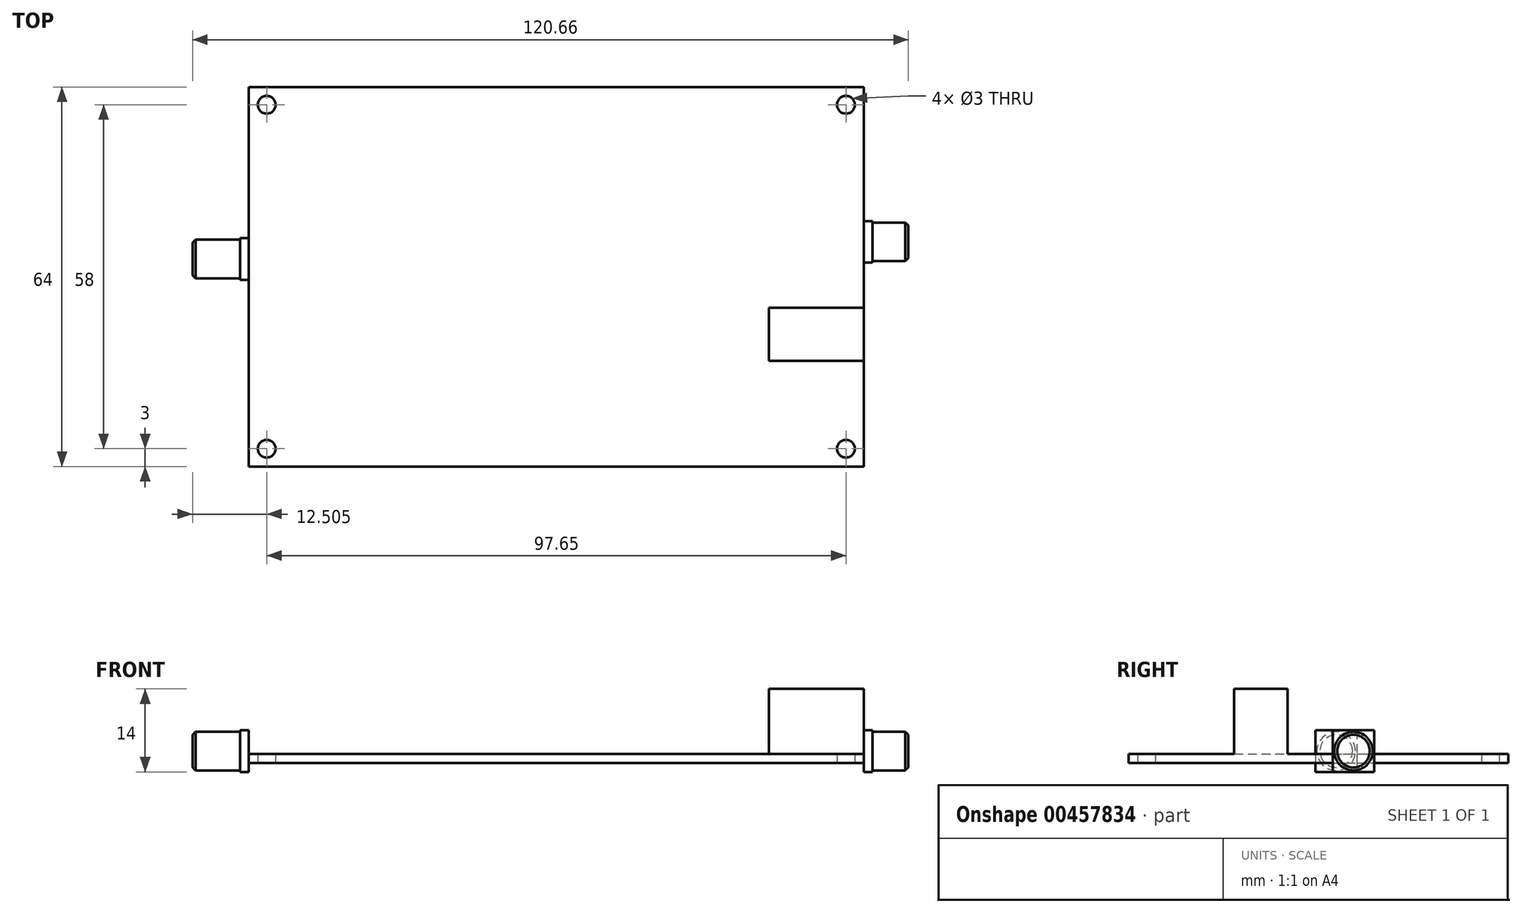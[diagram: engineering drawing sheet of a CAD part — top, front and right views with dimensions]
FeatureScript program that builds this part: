
annotation { "Feature Type Name" : "Feature", "Feature Type Description" : "" }
export const myFeature = defineFeature(function(context is Context, id is Id, definition is map)
    precondition{}
    {
        {
            var Q0;
            Q0=qCreatedBy(makeId("Top.planeOp"),FACE);
            var sketch = newSketch(context, id + "F0", { "sketchPlane" : qUnion([Q0])});
            skLineSegment(sketch, "E0.bottom", {"start": v(51.83, -32) * mm, "end": v(-51.82, -32) * mm});
            skLineSegment(sketch, "E0.top", {"start": v(51.83, 32) * mm, "end": v(-51.82, 32) * mm});
            skLineSegment(sketch, "E0.left", {"start": v(51.83, -32) * mm, "end": v(51.83, 32) * mm});
            skLineSegment(sketch, "E0.right", {"start": v(-51.83, -32) * mm, "end": v(-51.83, 32) * mm});
            skPoint(sketch, "E0.middle", {"position": v(0, 0) * mm});
            skCircle(sketch, "E1", {"center": v(-48.83, -29) * mm, "radius": 1.5 * mm});
            skCircle(sketch, "E2", {"center": v(-48.83, 29) * mm, "radius": 1.5 * mm});
            skCircle(sketch, "E3", {"center": v(48.82, 29) * mm, "radius": 1.5 * mm});
            skCircle(sketch, "E4", {"center": v(48.82, -29) * mm, "radius": 1.5 * mm});
            skSolve(sketch);
        }
        {
            var Q0;
            Q0=makeQuery(id+"F0.imprint","IMPRINT",FACE,{"disambiguationData":[TD([[makeQuery(id+"F0.imprint","IMPRINT",EDGE,{"derivedFrom":sQuery(id+"F0.wireOp",EDGE,"E0.bottom")}),-1.0]])]});
            extrude(context, id + "F1", {"entities" : qUnion([Q0]), "depth" : 1.5 * mm});
        }
        {
            var Q0;
            Q0=makeQuery(id+"F1.opExtrude","SWEPT_FACE",FACE,{"disambiguationData":[OSD([sQuery(id+"F0.wireOp",EDGE,"E0.left")])]});
            var sketch = newSketch(context, id + "F2", { "sketchPlane" : qUnion([Q0])});
            skLineSegment(sketch, "E5.bottom", {"start": v(-14.2, 1.5) * mm, "end": v(-5.2, 1.5) * mm});
            skLineSegment(sketch, "E5.top", {"start": v(-14.2, 12.5) * mm, "end": v(-5.2, 12.5) * mm});
            skLineSegment(sketch, "E5.left", {"start": v(-14.2, 1.5) * mm, "end": v(-14.2, 12.5) * mm});
            skLineSegment(sketch, "E5.right", {"start": v(-5.2, 1.5) * mm, "end": v(-5.2, 12.5) * mm});
            skSolve(sketch);
        }
        {
            var Q0;
            Q0=makeQuery(id+"F2.imprint","IMPRINT",FACE,{"disambiguationData":[TD([[makeQuery(id+"F2.imprint","IMPRINT",EDGE,{"derivedFrom":sQuery(id+"F2.wireOp",EDGE,"E5.bottom")}),1.0]])]});
            extrude(context, id + "F3", {"entities" : qUnion([Q0]), "operationType" : NewBodyOperationType.ADD, "oppositeDirection" : true, "depth" : 16 * mm});
        }
        {
            var Q0;
            {var subQ3=sQuery(id+"F2.wireOp",EDGE,"E5.bottom");Q0=makeQuery(id+"F2.imprint","IMPRINT",FACE,{"disambiguationData":[TD([[makeQuery(id+"F2.imprint","IMPRINT",EDGE,{"derivedFrom":subQ3}),-1.0]])]});}
            var sketch = newSketch(context, id + "F4", { "sketchPlane" : qUnion([Q0])});
            skLineSegment(sketch, "E6.bottom", {"start": v(2.4, 5.5) * mm, "end": v(9.4, 5.5) * mm});
            skLineSegment(sketch, "E6.top", {"start": v(2.4, -1.5) * mm, "end": v(9.4, -1.5) * mm});
            skLineSegment(sketch, "E6.left", {"start": v(2.4, 5.5) * mm, "end": v(2.4, -1.5) * mm});
            skLineSegment(sketch, "E6.right", {"start": v(9.4, 5.5) * mm, "end": v(9.4, -1.5) * mm});
            skSolve(sketch);
        }
        {
            var Q0;
            Q0 = qSketchRegion(id + "F4", true);
            var Q1;
            {var subQ0=sQuery(id+"F4.wireOp",EDGE,"E6.bottom");Q1=makeQuery(id+"F4.imprint","IMPRINT",FACE,{"disambiguationData":[TD([[makeQuery(id+"F4.imprint","IMPRINT",EDGE,{"derivedFrom":subQ0}),-1.0]])]});}
            extrude(context, id + "F5", {"entities" : qUnion([Q0, Q1]), "operationType" : NewBodyOperationType.ADD, "depth" : 1.5 * mm});
        }
        {
            var Q0;
            Q0=makeQuery(id+"F5.opExtrude","CAP_FACE",FACE,{"disambiguationData":[OSD([sQuery(id+"F4.wireOp",EDGE,"E6.bottom"),sQuery(id+"F4.wireOp",EDGE,"E6.top"),sQuery(id+"F4.wireOp",EDGE,"E6.left"),sQuery(id+"F4.wireOp",EDGE,"E6.right")])],"isStart":false});
            var sketch = newSketch(context, id + "F6", { "sketchPlane" : qUnion([Q0])});
            skCircle(sketch, "E7", {"center": v(5.9, 2) * mm, "radius": 3.25 * mm});
            skSolve(sketch);
        }
        {
            var Q0;
            Q0=makeQuery(id+"F6.imprint","IMPRINT",FACE,{"disambiguationData":[TD([[makeQuery(id+"F6.imprint","IMPRINT",EDGE,{"derivedFrom":sQuery(id+"F6.wireOp",EDGE,"E7")}),1.0]])]});
            extrude(context, id + "F7", {"entities" : qUnion([Q0]), "operationType" : NewBodyOperationType.ADD, "depth" : 6 * mm});
        }
        {
            var Q0;
            Q0=makeQuery(id+"F1.opExtrude","SWEPT_FACE",FACE,{"disambiguationData":[OSD([sQuery(id+"F0.wireOp",EDGE,"E0.right")])]});
            var sketch = newSketch(context, id + "F8", { "sketchPlane" : qUnion([Q0])});
            skLineSegment(sketch, "E8.bottom", {"start": v(-6.5, 5.5) * mm, "end": v(0.5, 5.5) * mm});
            skLineSegment(sketch, "E8.top", {"start": v(-6.5, -1.5) * mm, "end": v(0.5, -1.5) * mm});
            skLineSegment(sketch, "E8.left", {"start": v(-6.5, 5.5) * mm, "end": v(-6.5, -1.5) * mm});
            skLineSegment(sketch, "E8.right", {"start": v(0.5, 5.5) * mm, "end": v(0.5, -1.5) * mm});
            skSolve(sketch);
        }
        {
            var Q0;
            {var subQ0=sQuery(id+"F8.wireOp",EDGE,"E8.bottom");Q0=makeQuery(id+"F8.imprint","IMPRINT",FACE,{"disambiguationData":[TD([[makeQuery(id+"F8.imprint","IMPRINT",EDGE,{"derivedFrom":subQ0}),-1.0]])]});}
            var Q1;
            {var subQ0=sQuery(id+"F8.wireOp",EDGE,"E8.left");var subQ1=sQuery(id+"F0.wireOp",EDGE,"E0.right");var subQ2=makeQuery(id+"F1.opExtrude","CAP_EDGE",EDGE,{"disambiguationData":[OSD([subQ1])],"isStart":false});var subQ3=makeQuery(id+"F8.imprint","INTERSECT",VERTEX,{"derivedFrom":[subQ2,subQ0]});Q1=makeQuery(id+"F8.imprint","IMPRINT",FACE,{"disambiguationData":[TD([[makeQuery(id+"F8.imprint","IMPRINT",EDGE,{"disambiguationData":[TD([[subQ3,-1.0]])],"derivedFrom":subQ0}),1.0]])]});}
            var Q2;
            {var subQ0=sQuery(id+"F8.wireOp",EDGE,"E8.top");Q2=makeQuery(id+"F8.imprint","IMPRINT",FACE,{"disambiguationData":[TD([[makeQuery(id+"F8.imprint","IMPRINT",EDGE,{"derivedFrom":subQ0}),1.0]])]});}
            extrude(context, id + "F9", {"entities" : qUnion([Q0, Q1, Q2]), "operationType" : NewBodyOperationType.ADD, "depth" : 1.5 * mm});
        }
        {
            var Q0;
            Q0=makeQuery(id+"F9.opExtrude","CAP_FACE",FACE,{"disambiguationData":[OSD([sQuery(id+"F8.wireOp",EDGE,"E8.bottom"),sQuery(id+"F8.wireOp",EDGE,"E8.top"),sQuery(id+"F8.wireOp",EDGE,"E8.left"),sQuery(id+"F8.wireOp",EDGE,"E8.right")])],"isStart":false});
            var sketch = newSketch(context, id + "F10", { "sketchPlane" : qUnion([Q0])});
            skCircle(sketch, "E9", {"center": v(-3, 2) * mm, "radius": 3.25 * mm});
            skSolve(sketch);
        }
        {
            var Q0;
            Q0=makeQuery(id+"F10.imprint","IMPRINT",FACE,{"disambiguationData":[TD([[makeQuery(id+"F10.imprint","IMPRINT",EDGE,{"derivedFrom":sQuery(id+"F10.wireOp",EDGE,"E9")}),1.0]])]});
            extrude(context, id + "F11", {"entities" : qUnion([Q0]), "operationType" : NewBodyOperationType.ADD, "depth" : 8 * mm});
        }
        {
            var Q0;
            Q0=makeQuery(id+"F11.opExtrude","CAP_EDGE",EDGE,{"disambiguationData":[OSD([sQuery(id+"F10.wireOp",EDGE,"E9")])],"isStart":false});
            chamfer(context, id + "F12", {"entities" : qUnion([Q0]), "width" : 0.5 * mm, "tangentPropagation" : true});
        }
        {
            var Q0;
            Q0=makeQuery(id+"F7.opExtrude","CAP_EDGE",EDGE,{"disambiguationData":[OSD([sQuery(id+"F6.wireOp",EDGE,"E7")])],"isStart":false});
            chamfer(context, id + "F13", {"entities" : qUnion([Q0]), "width" : 0.5 * mm, "tangentPropagation" : true});
        }
    });
